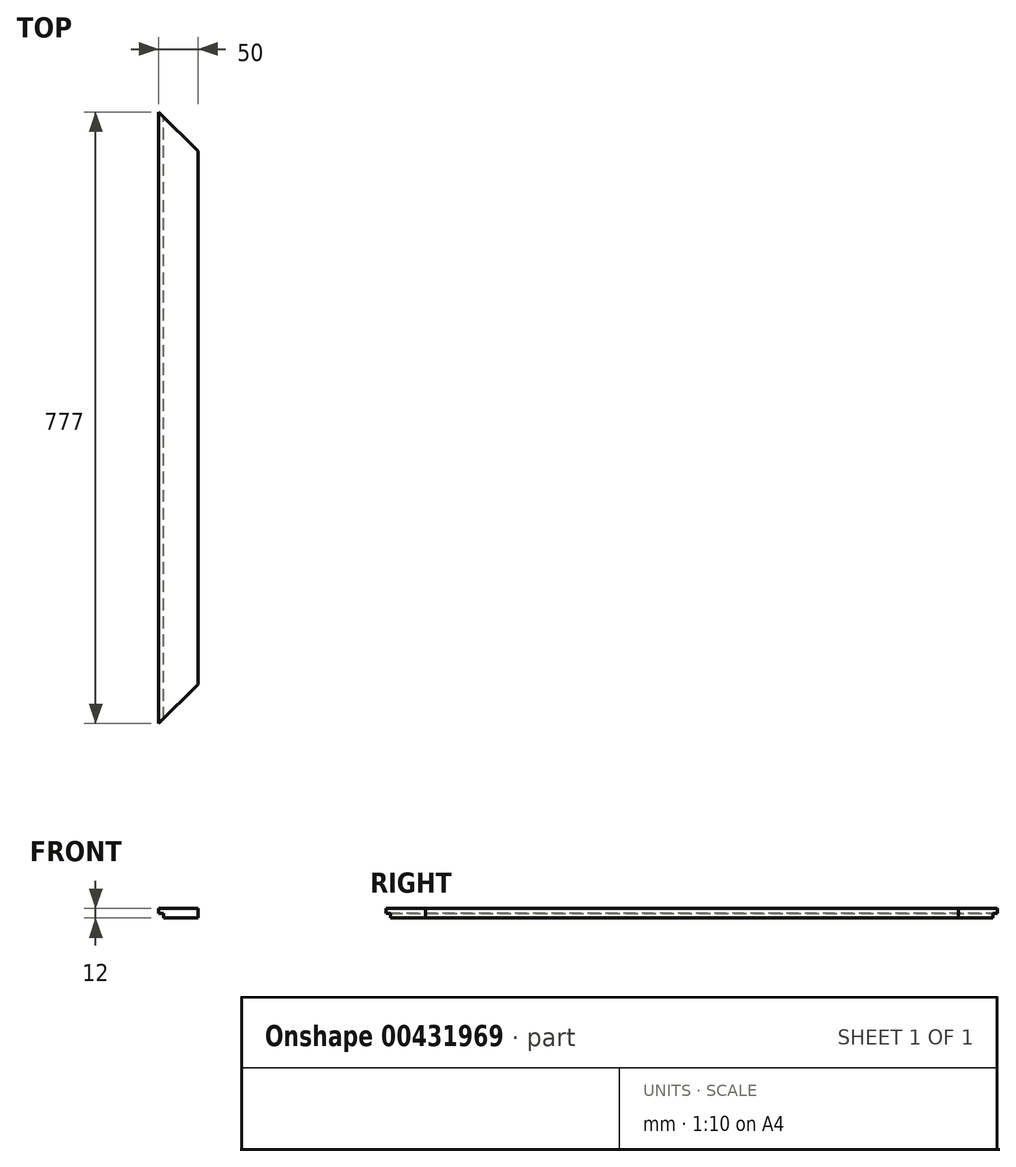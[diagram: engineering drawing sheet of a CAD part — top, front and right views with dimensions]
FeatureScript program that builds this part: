
annotation { "Feature Type Name" : "Feature", "Feature Type Description" : "" }
export const myFeature = defineFeature(function(context is Context, id is Id, definition is map)
    precondition{}
    {
        {
            var Q0;
            Q0=qCreatedBy(makeId("Top.planeOp"),FACE);
            var sketch = newSketch(context, id + "F0", { "sketchPlane" : qUnion([Q0])});
            skLineSegment(sketch, "E0.bottom", {"start": v(-25, 388.5) * mm, "end": v(25, 388.5) * mm});
            skLineSegment(sketch, "E0.top", {"start": v(-25, -388.5) * mm, "end": v(25, -388.5) * mm});
            skLineSegment(sketch, "E0.left", {"start": v(-25, 388.5) * mm, "end": v(-25, -388.5) * mm});
            skLineSegment(sketch, "E0.right", {"start": v(25, 388.5) * mm, "end": v(25, -388.5) * mm});
            skPoint(sketch, "E0.middle", {"position": v(0, 0) * mm});
            skSolve(sketch);
        }
        {
            var Q0;
            Q0=qSketchRegion(id+"F0",true);
            extrude(context, id + "F1", {"entities" : qUnion([Q0]), "depth" : 12 * mm, "offsetDistance" : 25 * mm});
        }
        {
            var Q0;
            Q0=makeQuery(id+"F1.opExtrude","CAP_FACE",FACE,{"disambiguationData":[OSD([sQuery(id+"F0.wireOp",EDGE,"E0.bottom"),sQuery(id+"F0.wireOp",EDGE,"E0.top"),sQuery(id+"F0.wireOp",EDGE,"E0.left"),sQuery(id+"F0.wireOp",EDGE,"E0.right")])],"isStart":true});
            var sketch = newSketch(context, id + "F2", { "sketchPlane" : qUnion([Q0])});
            skLineSegment(sketch, "E1.bottom", {"start": v(-25, 388.5) * mm, "end": v(-19, 388.5) * mm});
            skLineSegment(sketch, "E1.top", {"start": v(-25, -388.5) * mm, "end": v(-19, -388.5) * mm});
            skLineSegment(sketch, "E1.left", {"start": v(-25, 388.5) * mm, "end": v(-25, -388.5) * mm});
            skLineSegment(sketch, "E1.right", {"start": v(-19, 388.5) * mm, "end": v(-19, -388.5) * mm});
            skSolve(sketch);
        }
        {
            var Q0;
            Q0=qSketchRegion(id+"F2",true);
            extrude(context, id + "F3", {"entities" : qUnion([Q0]), "operationType" : NewBodyOperationType.REMOVE, "oppositeDirection" : true, "depth" : 6 * mm, "offsetDistance" : 25 * mm});
        }
        {
            var Q0;
            Q0=makeQuery(id+"F1.opExtrude","CAP_FACE",FACE,{"disambiguationData":[OSD([sQuery(id+"F0.wireOp",EDGE,"E0.bottom"),sQuery(id+"F0.wireOp",EDGE,"E0.top"),sQuery(id+"F0.wireOp",EDGE,"E0.left"),sQuery(id+"F0.wireOp",EDGE,"E0.right")])],"isStart":false});
            var sketch = newSketch(context, id + "F4", { "sketchPlane" : qUnion([Q0])});
            skLineSegment(sketch, "E2", {"start": v(-25, -388.5) * mm, "end": v(25, -338.5) * mm});
            skLineSegment(sketch, "E3", {"start": v(25, -338.5) * mm, "end": v(25, -388.5) * mm});
            skLineSegment(sketch, "E4", {"start": v(25, -388.5) * mm, "end": v(-25, -388.5) * mm});
            skSolve(sketch);
        }
        {
            var Q0;
            Q0=qSketchRegion(id+"F4",true);
            extrude(context, id + "F5", {"entities" : qUnion([Q0]), "operationType" : NewBodyOperationType.REMOVE, "endBound" : BoundingType.UP_TO_NEXT, "oppositeDirection" : true, "depth" : 25 * mm});
        }
        {
            var Q0;
            Q0=makeQuery(id+"F1.opExtrude","CAP_FACE",FACE,{"disambiguationData":[OSD([sQuery(id+"F0.wireOp",EDGE,"E0.bottom"),sQuery(id+"F0.wireOp",EDGE,"E0.top"),sQuery(id+"F0.wireOp",EDGE,"E0.left"),sQuery(id+"F0.wireOp",EDGE,"E0.right")])],"isStart":false});
            var sketch = newSketch(context, id + "F6", { "sketchPlane" : qUnion([Q0])});
            skLineSegment(sketch, "E5", {"start": v(-25, 388.5) * mm, "end": v(25, 338.5) * mm});
            skLineSegment(sketch, "E6", {"start": v(25, 338.5) * mm, "end": v(25, 388.5) * mm});
            skLineSegment(sketch, "E7", {"start": v(25, 388.5) * mm, "end": v(-25, 388.5) * mm});
            skSolve(sketch);
        }
        {
            var Q0;
            Q0=qSketchRegion(id+"F6",true);
            extrude(context, id + "F7", {"entities" : qUnion([Q0]), "operationType" : NewBodyOperationType.REMOVE, "endBound" : BoundingType.UP_TO_NEXT, "oppositeDirection" : true, "depth" : 25 * mm});
        }
    });
